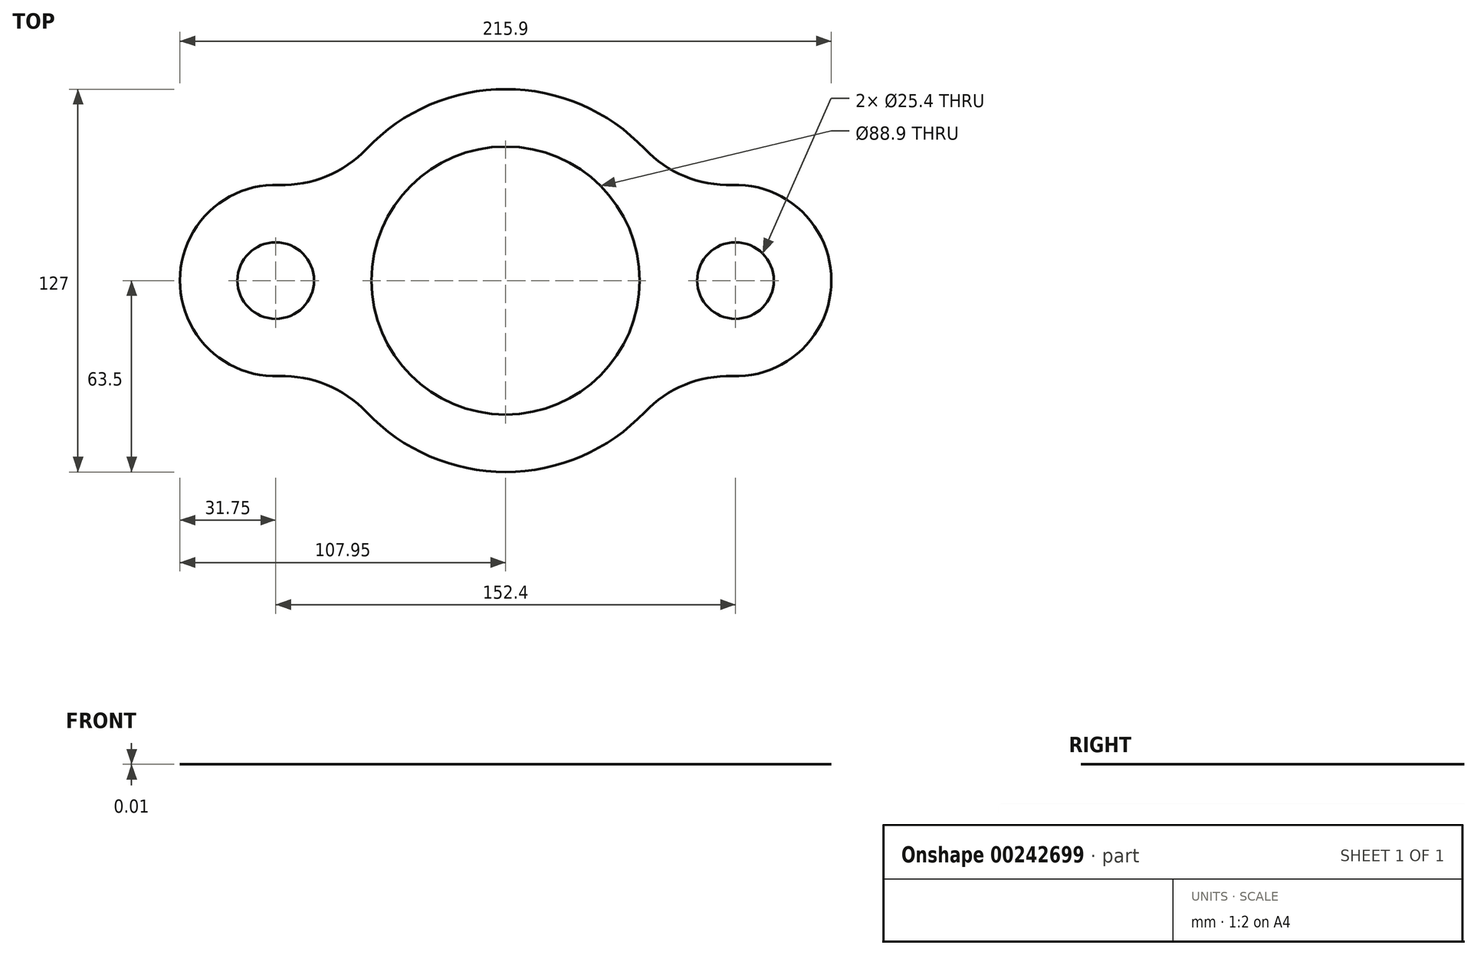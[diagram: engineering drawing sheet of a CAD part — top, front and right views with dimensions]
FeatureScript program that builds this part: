
annotation { "Feature Type Name" : "Feature", "Feature Type Description" : "" }
export const myFeature = defineFeature(function(context is Context, id is Id, definition is map)
    precondition{}
    {
        {
            var Q0;
            Q0=qCreatedBy(makeId("Top.planeOp"),FACE);
            var sketch = newSketch(context, id + "F0", { "sketchPlane" : qUnion([Q0])});
            skArc(sketch, "E0", {"start": v(-46.14, -43.63) * mm, "mid": v(0, -63.5) * mm, "end": v(46.14, -43.63) * mm});
            skCircle(sketch, "E1", {"center": v(0, 0) * mm, "radius": 44.45 * mm});
            skArc(sketch, "E2", {"start": v(75.12, -31.73) * mm, "mid": v(107.95, 0) * mm, "end": v(75.12, 31.73) * mm});
            skCircle(sketch, "E3", {"center": v(76.2, 0) * mm, "radius": 12.7 * mm});
            skArc(sketch, "E4", {"start": v(-75.12, 31.73) * mm, "mid": v(-107.95, 0) * mm, "end": v(-75.12, -31.73) * mm});
            skCircle(sketch, "E5", {"center": v(-76.2, 0) * mm, "radius": 12.7 * mm});
            skPoint(sketch, "E6.visualSharp", {"position": v(-57.94, 25.98) * mm});
            skArc(sketch, "E6.filletArc", {"start": v(-75.12, 31.73) * mm, "mid": v(-59.35, 34.56) * mm, "end": v(-46.14, 43.63) * mm});
            skArc(sketch, "E7.trimOffspring", {"start": v(46.14, 43.63) * mm, "mid": v(0, 63.5) * mm, "end": v(-46.14, 43.63) * mm});
            skPoint(sketch, "E8.visualSharp", {"position": v(57.94, 25.98) * mm});
            skArc(sketch, "E8.filletArc", {"start": v(46.14, 43.63) * mm, "mid": v(59.35, 34.56) * mm, "end": v(75.12, 31.73) * mm});
            skPoint(sketch, "E9.visualSharp", {"position": v(57.94, -25.98) * mm});
            skArc(sketch, "E9.filletArc", {"start": v(75.12, -31.73) * mm, "mid": v(59.35, -34.56) * mm, "end": v(46.14, -43.63) * mm});
            skPoint(sketch, "E10.visualSharp", {"position": v(-57.94, -25.98) * mm});
            skArc(sketch, "E10.filletArc", {"start": v(-46.14, -43.63) * mm, "mid": v(-59.35, -34.56) * mm, "end": v(-75.12, -31.73) * mm});
            skSolve(sketch);
        }
        {
            var Q0;
            Q0=makeQuery(id+"F0.imprint","IMPRINT",FACE,{"disambiguationData":[TD([[makeQuery(id+"F0.imprint","IMPRINT",EDGE,{"derivedFrom":sQuery(id+"F0.wireOp",EDGE,"E0")}),1.0]])]});
            extrude(context, id + "F1", {"entities" : qUnion([Q0]), "depth" : 1 / 101.6 * mm});
        }
    });
